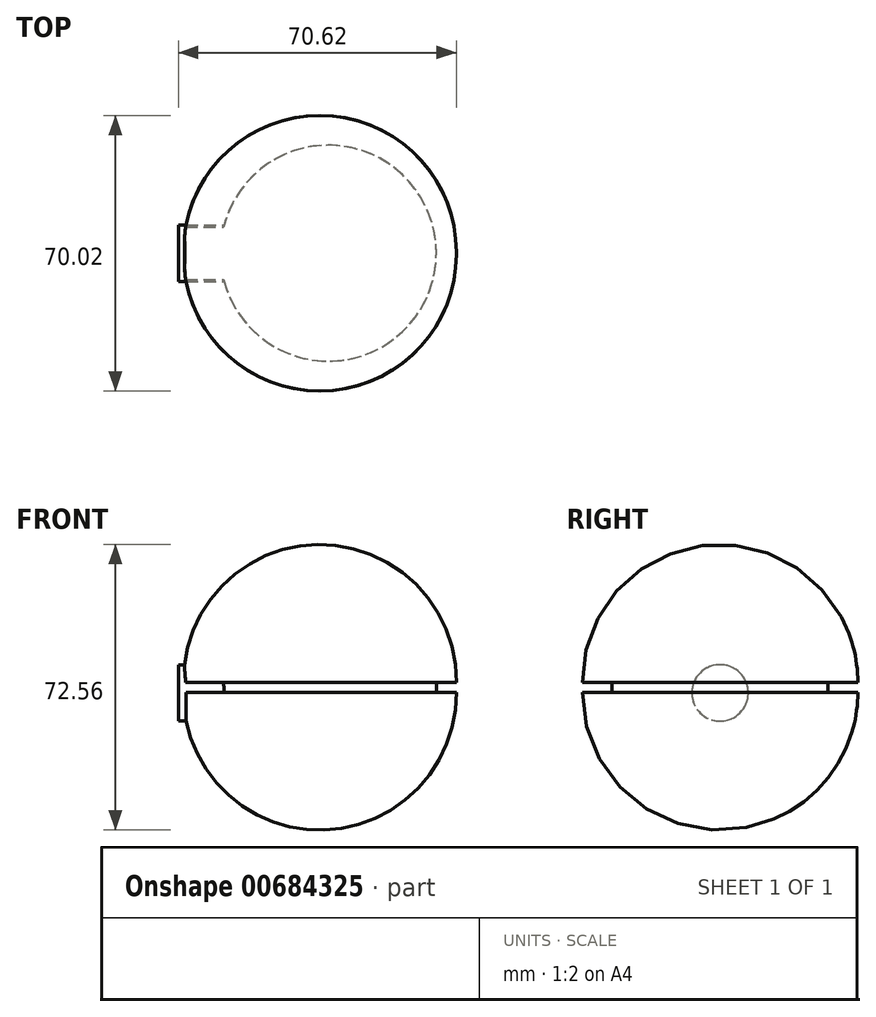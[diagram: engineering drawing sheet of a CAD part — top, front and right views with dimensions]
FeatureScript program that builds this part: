
annotation { "Feature Type Name" : "Feature", "Feature Type Description" : "" }
export const myFeature = defineFeature(function(context is Context, id is Id, definition is map)
    precondition{}
    {
        {
            var Q0;
            Q0=qCreatedBy(makeId("Top.planeOp"),FACE);
            var sketch = newSketch(context, id + "F0", { "sketchPlane" : qUnion([Q0])});
            skArc(sketch, "E0", {"start": v(-36.83, 0) * mm, "mid": v(-2.15, -35) * mm, "end": v(32.52, 0) * mm});
            skLineSegment(sketch, "E1", {"start": v(-36.83, 0) * mm, "end": v(32.52, 0) * mm});
            skSolve(sketch);
        }
        {
            var Q0;
            Q0 = qSketchRegion(id + "F0", true);
            var Q1;
            Q1=sQuery(id+"F0.wireOp",EDGE,"E1");
            revolve(context, id + "F1", {"entities" : qUnion([Q0]), "axis" : qUnion([Q1]), "revolveType" : RevolveType.ONE_DIRECTION, "oppositeDirection" : true, "angle" : 180 * degree});
        }
        {
            var Q0;
            Q0=qCreatedBy(makeId("Front.planeOp"),FACE);
            var sketch = newSketch(context, id + "F2", { "sketchPlane" : qUnion([Q0])});
            skLineSegment(sketch, "E2", {"start": v(-31.75, 0) * mm, "end": v(-31.75, -1.27) * mm});
            skLineSegment(sketch, "E3", {"start": v(-31.75, -1.27) * mm, "end": v(27.44, -1.27) * mm});
            skLineSegment(sketch, "E4", {"start": v(27.44, -1.27) * mm, "end": v(27.44, 0) * mm});
            skLineSegment(sketch, "E5", {"start": v(27.44, 0) * mm, "end": v(-31.75, 0) * mm});
            skLineSegment(sketch, "E6", {"start": v(0, 0) * mm, "end": v(0, -1.27) * mm});
            skSolve(sketch);
        }
        {
            var Q0;
            {var subQ0=sQuery(id+"F2.wireOp",EDGE,"E4");Q0=makeQuery(id+"F2.imprint","IMPRINT",FACE,{"disambiguationData":[TD([[makeQuery(id+"F2.imprint","IMPRINT",EDGE,{"derivedFrom":subQ0}),1.0]])]});}
            var Q1;
            Q1=sQuery(id+"F2.wireOp",EDGE,"E6");
            revolve(context, id + "F3", {"operationType" : NewBodyOperationType.ADD, "entities" : qUnion([Q0]), "axis" : qUnion([Q1]), "revolveType" : RevolveType.FULL});
        }
        {
            var Q0;
            Q0=makeQuery(id+"F1.opRevolve","SWEPT_BODY",BODY,{"disambiguationData":[OSD([sQuery(id+"F0.wireOp",EDGE,"E0"),sQuery(id+"F0.wireOp",EDGE,"E1")])]});
            var Q1;
            Q1=makeQuery(id+"F3.opRevolve","SWEPT_FACE",FACE,{"disambiguationData":[OSD([sQuery(id+"F2.wireOp",EDGE,"E3")])]});
            mirror(context, id + "F4", {"operationType" : NewBodyOperationType.ADD, "entities" : qUnion([Q0]), "mirrorPlane" : qUnion([Q1])});
        }
        {
            var Q0;
            Q0=qCreatedBy(makeId("Right.planeOp"),FACE);
            var sketch = newSketch(context, id + "F5", { "sketchPlane" : qUnion([Q0])});
            skPoint(sketch, "E7", {"position": v(0, -2.7) * mm});
            skCircle(sketch, "E8", {"center": v(0, -2.7) * mm, "radius": 7.16 * mm});
            skSolve(sketch);
        }
        {
            var Q0;
            Q0=sQuery(id+"F5.wireOp",EDGE,"E8");
            extrude(context, id + "F6", {"bodyType" : ToolBodyType.SURFACE, "surfaceEntities" : qUnion([Q0]), "oppositeDirection" : true, "depth" : 38.1 * mm, "offsetDistance" : 25.4 * mm});
        }
        {
            var Q0;
            Q0=qCreatedBy(makeId("Right.planeOp"),FACE);
            var sketch = newSketch(context, id + "F7", { "sketchPlane" : qUnion([Q0])});
            skCircle(sketch, "E9.0", {"center": v(0, -2.7) * mm, "radius": 7.16 * mm});
            skLineSegment(sketch, "E10", {"start": v(0, -2.7) * mm, "end": v(-0.75, 4.43) * mm});
            skSolve(sketch);
        }
        {
            var Q0;
            Q0 = qSketchRegion(id + "F7", true);
            extrude(context, id + "F8", {"entities" : qUnion([Q0]), "operationType" : NewBodyOperationType.ADD, "oppositeDirection" : true, "depth" : 38.1 * mm, "offsetDistance" : 25.4 * mm});
        }
    });
